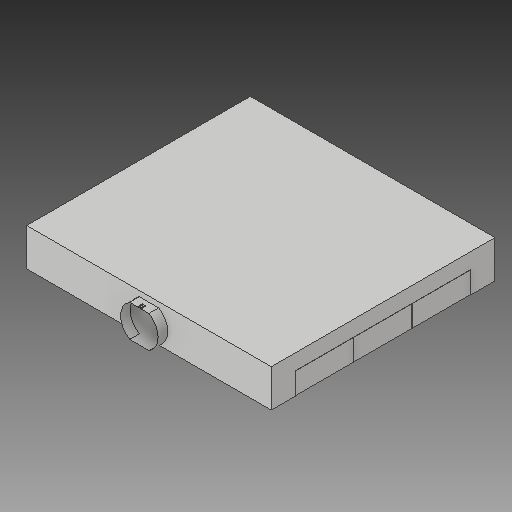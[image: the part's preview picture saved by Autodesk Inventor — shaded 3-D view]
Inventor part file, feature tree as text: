
AUTODESK INVENTOR PART (.ipt)
format: ipt  version: 2017 (Build 210142000, 142)  size: 330,240 bytes
history: native  units: in
note: dims shown in document units (in); Inventor stores cm internally (conversion verified against a paired STEP export)
features: extrude x6, sketch x5, delete_face x1
ambient origin geometry x8: Origin, YZ Plane, XZ Plane, XY Plane, X Axis, Y Axis, Z Axis, Center Point
bodies: Solid1 (feature_tree)
feature tree (12):
  extrude  "cubicals"  Depth=12.0in
  extrude  "floor"  Depth=2.5in
  extrude  "walls"  Depth=0.0833in
  sketch  "Sketch4"  dims[d10=0.0833in d95=0.0833in]
  extrude  "connection"  Depth=0.0833in
  extrude  "connection cut"  Depth=2.5in
  extrude  "ceiling"  Depth=2.5in
  delete_face  "Delete Face1"
  sketch  "Sketch2"  dims[d2=4.5in d3=0.0in d4=12.0in]
  sketch  "Sketch3"  dims[d5=8.0in d7=2.5in]
  sketch  "Sketch6"  dims[d97=0.0833in d98=0.0833in]
  sketch  "Sketch7"  dims[d99=12.0in d100=8.0in d102=0.0833in d103=0.0833in d104=0.0833in d105=0.0833in d106=12.0in d107=8.0in d109=0.0833in d110=0.0833in d111=0.0833in d112=0.0833in d113=2.5in d114=2.5in d115=3.0in d117=3.0in d118=6.0in d120=6.0in d121=1.0in d122=0.0in d128=1.0in d129=1.0in d130=1.0in d131=1.0in d132=1.0in d133=1.0in d134=7.7746in d135=0.0in d160=1.0in d161=0.0in d171=1.0in d172=0.0in d173=1.0in d174=0.0in d175=4.0in d176=0.5833in d177=3.8873in d178=3.8873in d179=1.7083in d180=0.0625in d181=0.0625in d182=1.6458in d183=0.25in d184=0.125in d185=0.0884in d186=45.0deg d187=3.3333in d188=1.0in d189=1.0in d190=0.125in]
